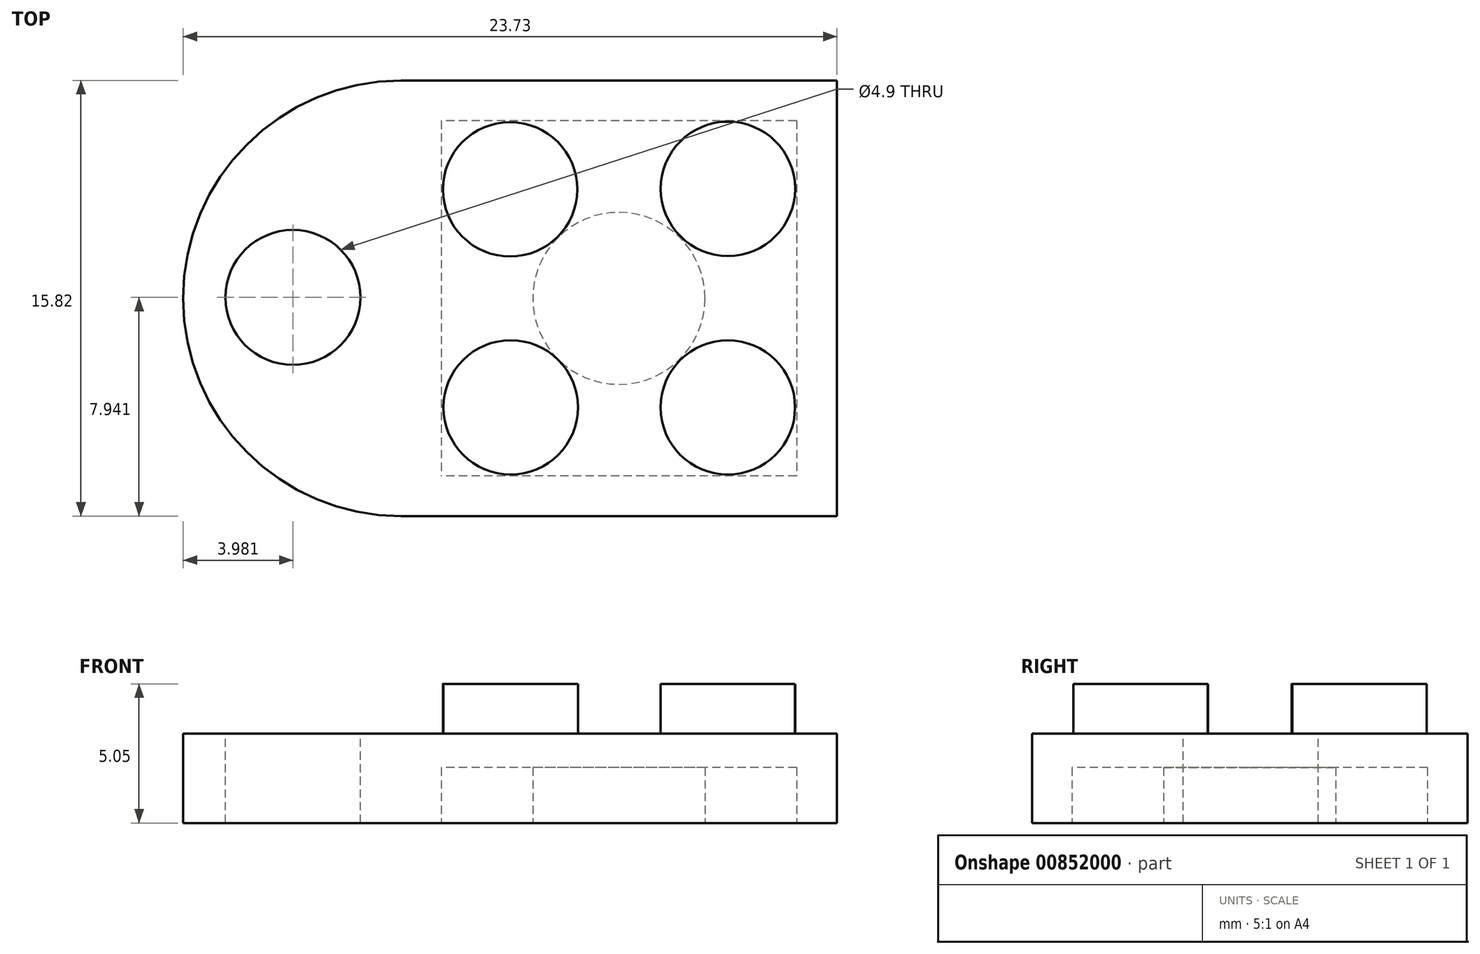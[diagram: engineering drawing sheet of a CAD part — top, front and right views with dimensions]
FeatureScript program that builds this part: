
annotation { "Feature Type Name" : "Feature", "Feature Type Description" : "" }
export const myFeature = defineFeature(function(context is Context, id is Id, definition is map)
    precondition{}
    {
        {
            var Q0;
            Q0=qCreatedBy(makeId("Top.planeOp"),FACE);
            var sketch = newSketch(context, id + "F0", { "sketchPlane" : qUnion([Q0])});
            skLineSegment(sketch, "E0.bottom", {"start": v(9.44, -9.43) * mm, "end": v(-6.38, -9.43) * mm});
            skLineSegment(sketch, "E0.top", {"start": v(9.44, 6.39) * mm, "end": v(-6.38, 6.39) * mm});
            skLineSegment(sketch, "E0.left", {"start": v(9.44, -9.43) * mm, "end": v(9.44, 6.39) * mm});
            skLineSegment(sketch, "E0.right", {"start": v(-6.38, -9.43) * mm, "end": v(-6.38, 6.39) * mm});
            skPoint(sketch, "E0.middle", {"position": v(1.53, -1.52) * mm});
            skArc(sketch, "E1", {"start": v(-6.38, 6.39) * mm, "mid": v(-14.3, -1.52) * mm, "end": v(-6.38, -9.43) * mm});
            skLineSegment(sketch, "E2", {"start": v(9.44, -9.43) * mm, "end": v(-6.38, 6.39) * mm, "construction": true});
            skLineSegment(sketch, "E3", {"start": v(9.44, 6.39) * mm, "end": v(-6.38, -9.43) * mm, "construction": true});
            skLineSegment(sketch, "E4.bottom", {"start": v(-4.92, 4.93) * mm, "end": v(7.98, 4.93) * mm, "construction": true});
            skLineSegment(sketch, "E4.top", {"start": v(-4.92, -7.97) * mm, "end": v(7.98, -7.97) * mm, "construction": true});
            skLineSegment(sketch, "E4.left", {"start": v(-4.92, 4.93) * mm, "end": v(-4.92, -7.97) * mm, "construction": true});
            skLineSegment(sketch, "E4.right", {"start": v(7.98, 4.93) * mm, "end": v(7.98, -7.97) * mm, "construction": true});
            skLineSegment(sketch, "E5", {"start": v(-13.52, -1.52) * mm, "end": v(-6.38, -1.52) * mm, "construction": true});
            skLineSegment(sketch, "E6", {"start": v(1.53, 13.4) * mm, "end": v(1.53, 6.39) * mm, "construction": true});
            skSolve(sketch);
        }
        {
            var Q0;
            Q0 = qSketchRegion(id + "F0", true);
            extrude(context, id + "F1", {"entities" : qUnion([Q0]), "depth" : 3.25 * mm, "offsetDistance" : 25 * mm});
        }
        {
            var Q0;
            Q0=makeQuery(id+"F1.opExtrude","CAP_FACE",FACE,{"disambiguationData":[OSD([sQuery(id+"F0.wireOp",EDGE,"E0.bottom"),sQuery(id+"F0.wireOp",EDGE,"E0.top"),sQuery(id+"F0.wireOp",EDGE,"E0.left"),sQuery(id+"F0.wireOp",EDGE,"E1")])],"isStart":false});
            var sketch = newSketch(context, id + "F2", { "sketchPlane" : qUnion([Q0])});
            skCircle(sketch, "E7", {"center": v(-2.42, 2.44) * mm, "radius": 2.44 * mm});
            skCircle(sketch, "E8", {"center": v(5.48, 2.46) * mm, "radius": 2.44 * mm});
            skCircle(sketch, "E9", {"center": v(5.48, -5.48) * mm, "radius": 2.44 * mm});
            skCircle(sketch, "E10", {"center": v(-2.4, -5.48) * mm, "radius": 2.44 * mm});
            skSolve(sketch);
        }
        {
            var Q0;
            Q0 = qSketchRegion(id + "F2", true);
            extrude(context, id + "F3", {"entities" : qUnion([Q0]), "operationType" : NewBodyOperationType.ADD, "depth" : 1.8 * mm, "offsetDistance" : 25 * mm});
        }
        {
            var Q0;
            Q0=makeQuery(id+"F0.imprint","IMPRINT",FACE,{"disambiguationData":[TD([[makeQuery(id+"F0.imprint","IMPRINT",EDGE,{"derivedFrom":sQuery(id+"F0.wireOp",EDGE,"E0.bottom")}),-1.0]])]});
            var sketch = newSketch(context, id + "F4", { "sketchPlane" : qUnion([Q0])});
            skLineSegment(sketch, "E11.bottom", {"start": v(7.98, 4.93) * mm, "end": v(-4.92, 4.93) * mm});
            skLineSegment(sketch, "E11.top", {"start": v(7.98, -7.97) * mm, "end": v(-4.92, -7.97) * mm});
            skLineSegment(sketch, "E11.left", {"start": v(7.98, 4.93) * mm, "end": v(7.98, -7.97) * mm});
            skLineSegment(sketch, "E11.right", {"start": v(-4.92, 4.93) * mm, "end": v(-4.92, -7.97) * mm});
            skPoint(sketch, "E11.middle", {"position": v(1.53, -1.52) * mm});
            skCircle(sketch, "E12", {"center": v(1.53, -1.52) * mm, "radius": 3.12 * mm});
            skSolve(sketch);
        }
        {
            var Q0;
            Q0 = qSketchRegion(id + "F4", true);
            extrude(context, id + "F5", {"entities" : qUnion([Q0]), "operationType" : NewBodyOperationType.REMOVE, "depth" : 2 * mm, "offsetDistance" : 25 * mm});
        }
        {
            var Q0;
            Q0=makeQuery(id+"F1.opExtrude","CAP_FACE",FACE,{"disambiguationData":[OSD([sQuery(id+"F0.wireOp",EDGE,"E0.bottom"),sQuery(id+"F0.wireOp",EDGE,"E0.top"),sQuery(id+"F0.wireOp",EDGE,"E0.left"),sQuery(id+"F0.wireOp",EDGE,"E1")])],"isStart":false});
            var sketch = newSketch(context, id + "F6", { "sketchPlane" : qUnion([Q0])});
            skCircle(sketch, "E13", {"center": v(-10.3, -1.49) * mm, "radius": 2.45 * mm});
            skSolve(sketch);
        }
        {
            var Q0;
            Q0 = qSketchRegion(id + "F6", true);
            extrude(context, id + "F7", {"entities" : qUnion([Q0]), "operationType" : NewBodyOperationType.REMOVE, "oppositeDirection" : true, "depth" : 25 * mm, "offsetDistance" : 25 * mm});
        }
    });
